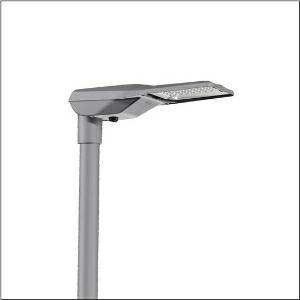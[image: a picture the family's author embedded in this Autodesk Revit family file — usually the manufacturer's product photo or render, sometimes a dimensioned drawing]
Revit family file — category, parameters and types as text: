
# Revit family: streetlight_sl_21_iq_mini___p0_5a_5xe2v31u08hb_fe50
name_source: partatom
category: Lighting Fixtures
units: mm (PartAtom-declared; Revit-internal decimal feet)

## family parameters
Cut with Voids When Loaded = No
Host = Face
Light Source = No
Part Type = Normal
Room Calculation Point = No
Round Connector Dimension = Use Diameter
Shared = No

## types (1)
- --- (1 x LED, 9580 lm, 71 W, 3000K)
    Apparent Load = 71 VA
    CIE Flux Codes = 37 73 96 100 100
    Color Rendering = 70
    Color Temperature = 3000K
    Default Elevation = 1800 mm
    Description = Streetlight SL 21 iQ mini, mast luminaire, primary light control with lens, of PMMA, primary optical cover: cover, of toughened safety glass, transparent, light distribution: P0.5a, light emission: direct distribution, primary light characteristic: asymmetric, installation type: post-top, side-entry, LED, High Power LED, rated luminous flux: 9.580lm, luminous efficacy: 135lm/W, light colour: 730, colour temperature: 3000K, control gear: iQ-Street Remote, D4i with power reduction, control: pre-setting: logarithmic dimming characteristic, Street-Remote, Auto-Match, Temp-Guard, Lumen-Switch, Night-Set, Smart-Wire, Light-Fading, Desk-Remote (wireless, voltage-free reading and setting of iQ features in the workshop via application-optimized NFC function/RFID function), optimised constant luminous flux control (CLO 2.0), mains connection: 220..240V, AC, 50/60Hz, start of lifetime: 71W, end of service life: 75W, reduction: 30W, luminaire housing, of diecast aluminium, powder-coated, Siteco® metallic grey (DB 702S), corrosivity category C5 mid according to DIN EN ISO 12944, please order mast flange separately, inclination adjustable: 0°, 5°, 10°, 15°, sealing non-destructively replaceable, multi-level sealing system, length: 628mm, width: 235mm, height: 110mm, mast flange for spigot size: 42mm (side-entry): 5XC10008XM4, 60/48mm (side-entry/post-top): 5XC10108XM2, 76/60mm (side-entry/post-top): 5XC10108XM1, mounting height: 4..8m, Smart Interface below, protection rating (complete): IP66, insulation class (complete): insulation class II (safety insulation), certification: CE, ENEC, ENEC+, VDE, impact resistance: IK09, permissible operating ambient temperature for outdoor applications: -40..+50°C, standard-compliant lighting for roads and squares, packaging unit: 1 piece

Light Distribution: P0.5a
    Height = 110 mm
    Lamp = 1 x LED
    Lamp Light Flux = 9580 lm
    Lamp Power = 71 W
    Lamp count = 1
    Length = 625 mm
    Luminous efficacy = 135 lm/W
    Manufacturer = Siteco
    ModVariant = No
    Model = 5XE2V31U08HB
    Number of Poles = 1
    OnlyDefault = Yes
    Power Factor = 1
    Product Name = Streetlight SL 21 iQ mini | P0.5a
    Product group = mast luminaire | pylon top
    ProductGroupID = 6100
    Protection Class = Protection class II
    Protection Degree = IP 66
    RLX_Detail_Level = 1
    RLX_Emergency_Light_Flux = 0 lm
    RLX_Emergency_Type = 0
    RLX_Emergency_Type_DB = No
    RlxData = <blob elided: 92065 chars, md5=a76e013d>
    Socket = socket
    Standby Power = 0 W
    System Light Flux = 9580 lm
    System Power = 71 W
    Type Comments = factory setting: luminous flux: 100 % | dim-lin: 254 | 716 mA
    Type Image = l_1003516.jpg
    URL = http://relux.com
    VarID = @adj_067642
    Voltage = 0 V
    Weight = 0.00 kg
    Width = 234 mm

## geometry (parser evidence)
native form markers: Blend x4, Sweep x10
no freeform markers — native parametric forms only
